# Revit family: e89b5312-f349-4bce-bb6a-03963eb088bd
name_source: partatom
category: Двери
revit_build: Autodesk Revit 2017 (Build: 20170118_1100(x64)
units: mm (PartAtom-declared; Revit-internal decimal feet)

## family parameters
Всегда вертикально = Да
Заголовок OmniClass = Doors
Номер OmniClass = 23.30.10.00
Общий = Нет
Основа = Стена
При загрузке вырезать с полостями = Нет
Точка расчета площади = Нет

## types (57) — shared parameters
270 = 270.00°
90 = 90.00°
Аналитическая конструкция = <Нет>
Высота фрамуги = 500 мм
Дверь = Да
Замыкание стены = По основе
Материал инженерного короба = <По категории>
Материал коробки = <По категории>
Материал панели фрамуги = <По категории>
Материал полотна двери = <По категории>
Материал ручки = <По категории>
Материал стекла = <По категории>
Монтажный зазор = 10 мм
О_Изображение = <Нет>
О_Материал = <По категории>
Проем = Нет
Угол открывания = 30.00°
Фрамуга = Нет
Функция = Внутренние слои
Ширина полотна двери = 50 мм

## per-type parameters (varying)
| type | Высота | Левое открывание | Правое открывание | Р_Высота | Р_Длина | Р_Толщина | Р_Ширина | Равнопольная | Тип двери | Толщина коробки | Толщина полотна двери | Ширина | Ширина большей створки | Ширина коробки | Ширина левой створки | Ширина правой створки |
| ДВ 21-6 | 2700 мм | Нет | Да | 2700 мм | 1700 мм | 30 мм | 1700 мм | Нет | 101_Двухстворчатая дверь | 100 мм | 30 мм | 1700 мм | 1050 мм | 50 мм | 1050 мм | 570 мм |
| ДВ 21-7 | 2100 мм | Нет | Да | 2100 мм | 700 мм | 5 мм | 700 мм | Нет | 101_Одностворчатая дверь сплошная | 10 мм | 5 мм | 700 мм | 0 мм | 25 мм | 0 мм | 670 мм |
| ДВ 21-6 Л | 2100 мм | Да | Нет | 2100 мм | 600 мм | 5 мм | 600 мм | Нет | 101_Одностворчатая дверь сплошная | 10 мм | 5 мм | 600 мм | 0 мм | 25 мм | 570 мм | 0 мм |
| ДВ 21-7 Л | 2100 мм | Да | Нет | 2100 мм | 700 мм | 5 мм | 700 мм | Нет | 101_Одностворчатая дверь сплошная | 10 мм | 5 мм | 700 мм | 0 мм | 25 мм | 670 мм | 0 мм |
| ДВ 21-8 | 2100 мм | Нет | Да | 2100 мм | 800 мм | 30 мм | 800 мм | Нет | 101_Одностворчатая дверь сплошная | 100 мм | 30 мм | 800 мм | 0 мм | 50 мм | 0 мм | 720 мм |
| ДВ 21-8 Л | 2100 мм | Да | Нет | 2100 мм | 800 мм | 30 мм | 800 мм | Нет | 101_Одностворчатая дверь сплошная | 100 мм | 30 мм | 800 мм | 0 мм | 50 мм | 720 мм | 0 мм |
| ДВ 21-9 | 2100 мм | Нет | Да | 2100 мм | 900 мм | 30 мм | 900 мм | Нет | 101_Одностворчатая дверь сплошная | 100 мм | 30 мм | 900 мм | 0 мм | 50 мм | 0 мм | 820 мм |
| ДВ 21-9 Л | 2100 мм | Да | Нет | 2100 мм | 900 мм | 30 мм | 900 мм | Нет | 101_Одностворчатая дверь сплошная | 100 мм | 30 мм | 900 мм | 0 мм | 50 мм | 820 мм | 0 мм |
| ДВ 21-10 | 2100 мм | Нет | Да | 2100 мм | 1000 мм | 30 мм | 1000 мм | Да | 101_Одностворчатая дверь сплошная | 100 мм | 30 мм | 1000 мм | 0 мм | 50 мм | 460 мм | 460 мм |
| ДВ 21-10 Л | 2100 мм | Да | Нет | 2100 мм | 1000 мм | 30 мм | 1000 мм | Да | 101_Одностворчатая дверь сплошная | 100 мм | 30 мм | 1000 мм | 0 мм | 50 мм | 460 мм | 460 мм |
| ДВ 21-11 | 2100 мм | Нет | Да | 2100 мм | 1100 мм | 30 мм | 1100 мм | Да | 101_Одностворчатая дверь сплошная | 100 мм | 30 мм | 1100 мм | 0 мм | 50 мм | 510 мм | 510 мм |
| ДВ 21-11 Л | 2100 мм | Да | Нет | 2100 мм | 1100 мм | 30 мм | 1100 мм | Да | 101_Одностворчатая дверь сплошная | 100 мм | 30 мм | 1100 мм | 0 мм | 50 мм | 510 мм | 510 мм |
| ДВ 27-6 | 2700 мм | Нет | Да | 2700 мм | 600 мм | 5 мм | 600 мм | Нет | 101_Одностворчатая дверь сплошная | 10 мм | 5 мм | 600 мм | 0 мм | 25 мм | 0 мм | 570 мм |
| ДВ 27-6 Л | 2700 мм | Да | Нет | 2700 мм | 600 мм | 5 мм | 600 мм | Нет | 101_Одностворчатая дверь сплошная | 10 мм | 5 мм | 600 мм | 0 мм | 25 мм | 570 мм | 0 мм |
| ДВ 27-7 | 2700 мм | Нет | Да | 2700 мм | 700 мм | 30 мм | 700 мм | Нет | 101_Одностворчатая дверь сплошная | 100 мм | 30 мм | 700 мм | 0 мм | 50 мм | 0 мм | 620 мм |
| ДВ 27-7 Л | 2700 мм | Да | Нет | 2700 мм | 700 мм | 30 мм | 700 мм | Нет | 101_Одностворчатая дверь сплошная | 100 мм | 30 мм | 700 мм | 0 мм | 50 мм | 620 мм | 0 мм |
| ДВ 27-8 | 2700 мм | Нет | Да | 2700 мм | 800 мм | 30 мм | 800 мм | Нет | 101_Одностворчатая дверь сплошная | 100 мм | 30 мм | 800 мм | 0 мм | 50 мм | 0 мм | 720 мм |
| ДВ 27-8 Л | 2700 мм | Да | Нет | 2700 мм | 800 мм | 30 мм | 800 мм | Нет | 101_Одностворчатая дверь сплошная | 100 мм | 30 мм | 800 мм | 0 мм | 50 мм | 720 мм | 0 мм |
| ДВ 27-9 | 2700 мм | Нет | Да | 2700 мм | 900 мм | 30 мм | 900 мм | Нет | 101_Одностворчатая дверь сплошная | 100 мм | 30 мм | 900 мм | 0 мм | 50 мм | 0 мм | 820 мм |
| ДВ 27-9 Л | 2700 мм | Да | Нет | 2700 мм | 900 мм | 30 мм | 900 мм | Нет | 101_Одностворчатая дверь сплошная | 100 мм | 30 мм | 900 мм | 0 мм | 50 мм | 820 мм | 0 мм |
| ДВ 27-10 | 2700 мм | Нет | Да | 2700 мм | 1000 мм | 30 мм | 1000 мм | Нет | 101_Одностворчатая дверь сплошная | 100 мм | 30 мм | 1000 мм | 0 мм | 50 мм | 0 мм | 920 мм |
| ДВ 27-10 Л | 2700 мм | Да | Нет | 2700 мм | 1000 мм | 30 мм | 1000 мм | Нет | 101_Одностворчатая дверь сплошная | 100 мм | 30 мм | 1000 мм | 0 мм | 50 мм | 920 мм | 0 мм |
| ДВ 27-11 | 2700 мм | Нет | Да | 2700 мм | 1100 мм | 30 мм | 1100 мм | Нет | 101_Одностворчатая дверь сплошная | 100 мм | 30 мм | 1100 мм | 0 мм | 50 мм | 0 мм | 1020 мм |
| ДВ 27-11 Л | 2700 мм | Да | Нет | 2700 мм | 1100 мм | 30 мм | 1100 мм | Нет | 101_Одностворчатая дверь сплошная | 100 мм | 30 мм | 1100 мм | 0 мм | 50 мм | 1020 мм | 0 мм |
| ДВ 27-12 | 2700 мм | Нет | Да | 2700 мм | 1200 мм | 30 мм | 1200 мм | Нет | 101_Одностворчатая дверь сплошная | 100 мм | 30 мм | 1200 мм | 0 мм | 50 мм | 0 мм | 1120 мм |
| ДВ 27-12 Л | 2700 мм | Да | Нет | 2700 мм | 1200 мм | 30 мм | 1200 мм | Нет | 101_Одностворчатая дверь сплошная | 100 мм | 30 мм | 1200 мм | 0 мм | 50 мм | 1120 мм | 0 мм |
| ДВ 27-13 | 2700 мм | Нет | Да | 2700 мм | 1300 мм | 30 мм | 1300 мм | Нет | 101_Одностворчатая дверь сплошная | 100 мм | 30 мм | 1300 мм | 0 мм | 50 мм | 0 мм | 1220 мм |
| ДВ 27-13 Л | 2700 мм | Да | Нет | 2700 мм | 1300 мм | 30 мм | 1300 мм | Нет | 101_Одностворчатая дверь сплошная | 100 мм | 30 мм | 1300 мм | 0 мм | 50 мм | 1220 мм | 0 мм |
| ДВ 27-14 | 2700 мм | Нет | Да | 2700 мм | 1400 мм | 30 мм | 1400 мм | Нет | 101_Одностворчатая дверь сплошная | 100 мм | 30 мм | 1400 мм | 0 мм | 50 мм | 0 мм | 1320 мм |
| ДВ 27-14 Л | 2700 мм | Да | Нет | 2700 мм | 1400 мм | 30 мм | 1400 мм | Нет | 101_Одностворчатая дверь сплошная | 100 мм | 30 мм | 1400 мм | 0 мм | 50 мм | 1320 мм | 0 мм |
| ДВ 21-13 двустворчатая | 2100 мм | Нет | Да | 2100 мм | 1300 мм | 30 мм | 1300 мм | Нет | 101_Двухстворчатая дверь | 100 мм | 30 мм | 1300 мм | 840 мм | 50 мм | 840 мм | 380 мм |
| ДВ 21-13 Л двустворчатая | 2100 мм | Да | Нет | 2100 мм | 1300 мм | 30 мм | 1300 мм | Нет | 101_Двухстворчатая дверь | 100 мм | 30 мм | 1300 мм | 840 мм | 50 мм | 380 мм | 840 мм |
| ДВ 21-14 двустворчатая | 2100 мм | Нет | Да | 2100 мм | 1400 мм | 30 мм | 1400 мм | Нет | 101_Двухстворчатая дверь | 100 мм | 30 мм | 1400 мм | 920 мм | 50 мм | 920 мм | 400 мм |
| ДВ 21-14 Л двустворчатая | 2100 мм | Да | Нет | 2100 мм | 1400 мм | 30 мм | 1400 мм | Нет | 101_Двухстворчатая дверь | 100 мм | 30 мм | 1400 мм | 920 мм | 50 мм | 400 мм | 920 мм |
| ДВ 21-15 двустворчатая | 2100 мм | Нет | Да | 2100 мм | 1500 мм | 30 мм | 1500 мм | Нет | 101_Двухстворчатая дверь | 100 мм | 30 мм | 1500 мм | 1000 мм | 50 мм | 1000 мм | 420 мм |
| ДВ 21-15 Л двустворчатая | 2100 мм | Да | Нет | 2100 мм | 1500 мм | 30 мм | 1500 мм | Нет | 101_Двухстворчатая дверь | 100 мм | 30 мм | 1500 мм | 1000 мм | 50 мм | 420 мм | 1000 мм |
| ДВ 21-16 двустворчатая | 2100 мм | Нет | Да | 2100 мм | 1600 мм | 30 мм | 1600 мм | Нет | 101_Двухстворчатая дверь | 100 мм | 30 мм | 1600 мм | 1050 мм | 50 мм | 1050 мм | 470 мм |
| ДВ 21-16 Л двустворчатая | 2100 мм | Да | Нет | 2100 мм | 1600 мм | 30 мм | 1600 мм | Нет | 101_Двухстворчатая дверь | 100 мм | 30 мм | 1600 мм | 1050 мм | 50 мм | 470 мм | 1050 мм |
| ДВ 21-17 двустворчатая | 2100 мм | Нет | Да | 2100 мм | 1700 мм | 30 мм | 1700 мм | Нет | 101_Двухстворчатая дверь | 100 мм | 30 мм | 1700 мм | 1050 мм | 50 мм | 1050 мм | 570 мм |
| ДВ 21-17 Л двустворчатая | 2100 мм | Да | Нет | 2100 мм | 1700 мм | 30 мм | 1700 мм | Нет | 101_Двухстворчатая дверь | 100 мм | 30 мм | 1700 мм | 1050 мм | 50 мм | 570 мм | 1050 мм |
| ДВ 27-16 двустворчатая | 2700 мм | Нет | Да | 2700 мм | 1600 мм | 30 мм | 1600 мм | Нет | 101_Двухстворчатая дверь | 100 мм | 30 мм | 1600 мм | 1050 мм | 50 мм | 1050 мм | 470 мм |
| ДВ 27-16 Л двустворчатая | 2700 мм | Да | Нет | 2700 мм | 1600 мм | 30 мм | 1600 мм | Нет | 101_Двухстворчатая дверь | 100 мм | 30 мм | 1600 мм | 1050 мм | 50 мм | 470 мм | 1050 мм |
| ДВ 27-17 двустворчатая | 2700 мм | Нет | Да | 2700 мм | 1700 мм | 30 мм | 1700 мм | Нет | 101_Двухстворчатая дверь | 100 мм | 30 мм | 1700 мм | 1050 мм | 50 мм | 1050 мм | 570 мм |
| ДВ 27-17 Л двустворчатая | 2700 мм | Да | Нет | 2700 мм | 1700 мм | 30 мм | 1700 мм | Нет | 101_Двухстворчатая дверь | 100 мм | 30 мм | 1700 мм | 1050 мм | 50 мм | 570 мм | 1050 мм |
| ДВ 21-12 равнопольная | 2100 мм | Нет | Да | 2100 мм | 1200 мм | 30 мм | 1200 мм | Да | 101_Двухстворчатая дверь | 100 мм | 30 мм | 1200 мм | 700 мм | 50 мм | 560 мм | 560 мм |
| ДВ 21-13 равнопольная | 2100 мм | Нет | Да | 2100 мм | 1300 мм | 30 мм | 1300 мм | Да | 101_Двухстворчатая дверь | 100 мм | 30 мм | 1300 мм | 700 мм | 50 мм | 610 мм | 610 мм |
| ДВ 21-14 равнопольная | 2100 мм | Нет | Да | 2100 мм | 1400 мм | 30 мм | 1400 мм | Да | 101_Двухстворчатая дверь | 100 мм | 30 мм | 1400 мм | 700 мм | 50 мм | 660 мм | 660 мм |
| ДВ 21-15 равнопольная | 2100 мм | Нет | Да | 2100 мм | 1500 мм | 30 мм | 1500 мм | Да | 101_Двухстворчатая дверь | 100 мм | 30 мм | 1500 мм | 700 мм | 50 мм | 710 мм | 710 мм |
| ДВ 21-16 равнопольная | 2100 мм | Нет | Да | 2100 мм | 1600 мм | 30 мм | 1600 мм | Да | 101_Двухстворчатая дверь | 100 мм | 30 мм | 1600 мм | 700 мм | 50 мм | 760 мм | 760 мм |
| ДВ 27-16 равнопольная | 2700 мм | Нет | Да | 2700 мм | 1600 мм | 30 мм | 1600 мм | Да | 101_Двухстворчатая дверь | 100 мм | 30 мм | 1600 мм | 700 мм | 50 мм | 760 мм | 760 мм |
| ДВ 27-17 равнопольная | 2700 мм | Нет | Да | 2700 мм | 1700 мм | 30 мм | 1700 мм | Да | 101_Двухстворчатая дверь | 100 мм | 30 мм | 1700 мм | 700 мм | 50 мм | 810 мм | 810 мм |
| ДВ 27-18 равнопольная | 2700 мм | Нет | Да | 2700 мм | 1800 мм | 30 мм | 1800 мм | Да | 101_Двухстворчатая дверь | 100 мм | 30 мм | 1800 мм | 700 мм | 50 мм | 860 мм | 860 мм |
| ДВ 27-19 равнопольная | 2700 мм | Нет | Да | 2700 мм | 1900 мм | 30 мм | 1900 мм | Да | 101_Двухстворчатая дверь | 100 мм | 30 мм | 1900 мм | 700 мм | 50 мм | 910 мм | 910 мм |
| ДВ 27-20 равнопольная | 2700 мм | Нет | Да | 2700 мм | 2000 мм | 30 мм | 2000 мм | Да | 101_Двухстворчатая дверь | 100 мм | 30 мм | 2000 мм | 700 мм | 50 мм | 960 мм | 960 мм |
| ДВ 27-21 равнопольная | 2700 мм | Нет | Да | 2700 мм | 2100 мм | 30 мм | 2100 мм | Да | 101_Двухстворчатая дверь | 100 мм | 30 мм | 2100 мм | 700 мм | 50 мм | 1010 мм | 1010 мм |
| ДВ 27-22 равнопольная | 2700 мм | Нет | Да | 2700 мм | 2200 мм | 30 мм | 2200 мм | Да | 101_Двухстворчатая дверь | 100 мм | 30 мм | 2200 мм | 700 мм | 50 мм | 1060 мм | 1060 мм |
| ДВ 27-23 равнопольная | 2700 мм | Нет | Да | 2700 мм | 2300 мм | 30 мм | 2300 мм | Да | 101_Двухстворчатая дверь | 100 мм | 30 мм | 2300 мм | 700 мм | 50 мм | 1110 мм | 1110 мм |
